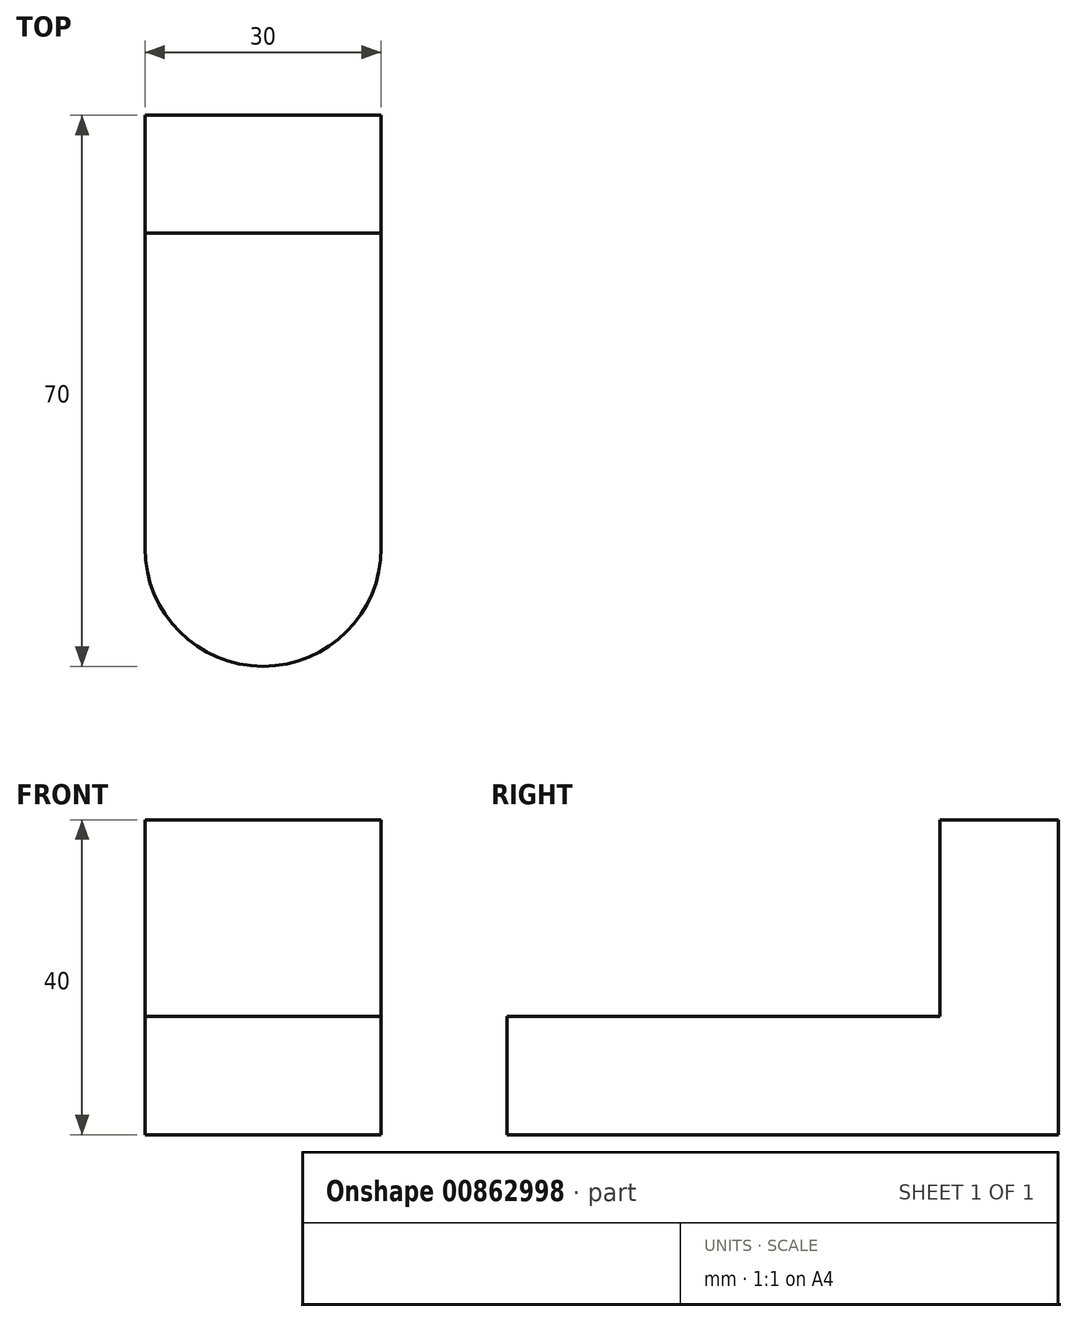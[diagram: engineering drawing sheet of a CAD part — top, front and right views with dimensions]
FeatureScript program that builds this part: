
annotation { "Feature Type Name" : "Feature", "Feature Type Description" : "" }
export const myFeature = defineFeature(function(context is Context, id is Id, definition is map)
    precondition{}
    {
        {
            var Q0;
            Q0=qCreatedBy(makeId("Top.planeOp"),FACE);
            var sketch = newSketch(context, id + "F0", { "sketchPlane" : qUnion([Q0])});
            skLineSegment(sketch, "E0.bottom", {"start": v(0, -35) * mm, "end": v(0, -35) * mm});
            skLineSegment(sketch, "E0.top", {"start": v(15, 35) * mm, "end": v(-15, 35) * mm});
            skLineSegment(sketch, "E0.left", {"start": v(15, -20) * mm, "end": v(15, 35) * mm});
            skLineSegment(sketch, "E0.right", {"start": v(-15, -20) * mm, "end": v(-15, 35) * mm});
            skPoint(sketch, "E0.middle", {"position": v(0, 0) * mm});
            skPoint(sketch, "E1.visualSharp", {"position": v(15, -35) * mm});
            skArc(sketch, "E1.filletArc", {"start": v(0, -35) * mm, "mid": v(10.6, -30.6) * mm, "end": v(15, -20) * mm});
            skPoint(sketch, "E2.visualSharp", {"position": v(-15, -35) * mm});
            skArc(sketch, "E2.filletArc", {"start": v(-15, -20) * mm, "mid": v(-10.6, -30.6) * mm, "end": v(0, -35) * mm});
            skSolve(sketch);
        }
        {
            var Q0;
            Q0=makeQuery(id+"F0.imprint","IMPRINT",FACE,{"disambiguationData":[TD([[makeQuery(id+"F0.imprint","IMPRINT",EDGE,{"derivedFrom":sQuery(id+"F0.wireOp",EDGE,"E0.top")}),1.0]])]});
            extrude(context, id + "F1", {"entities" : qUnion([Q0]), "depth" : 40 * mm, "offsetDistance" : 25 * mm});
        }
        {
            var Q0;
            Q0=makeQuery(id+"F1.opExtrude","CAP_FACE",FACE,{"disambiguationData":[OSD([sQuery(id+"F0.wireOp",EDGE,"E0.top"),sQuery(id+"F0.wireOp",EDGE,"E0.left"),sQuery(id+"F0.wireOp",EDGE,"E0.right"),sQuery(id+"F0.wireOp",EDGE,"E1.filletArc"),sQuery(id+"F0.wireOp",EDGE,"E2.filletArc")])],"isStart":false});
            var sketch = newSketch(context, id + "F2", { "sketchPlane" : qUnion([Q0])});
            skLineSegment(sketch, "E3", {"start": v(-15, 20) * mm, "end": v(15, 20) * mm});
            skLineSegment(sketch, "E4.left", {"start": v(-15, 20) * mm, "end": v(-15, -20) * mm});
            skLineSegment(sketch, "E4.right", {"start": v(15, 20) * mm, "end": v(15, -20) * mm});
            skArc(sketch, "E5", {"start": v(-15, -20) * mm, "mid": v(0, -35) * mm, "end": v(15, -20) * mm});
            skSolve(sketch);
        }
        {
            var Q0;
            Q0=makeQuery(id+"F2.imprint","IMPRINT",FACE,{"disambiguationData":[TD([[makeQuery(id+"F2.imprint","IMPRINT",EDGE,{"derivedFrom":sQuery(id+"F2.wireOp",EDGE,"E3")}),-1.0]])]});
            extrude(context, id + "F3", {"entities" : qUnion([Q0]), "operationType" : NewBodyOperationType.REMOVE, "oppositeDirection" : true, "depth" : 25 * mm, "offsetDistance" : 25 * mm});
        }
    });
